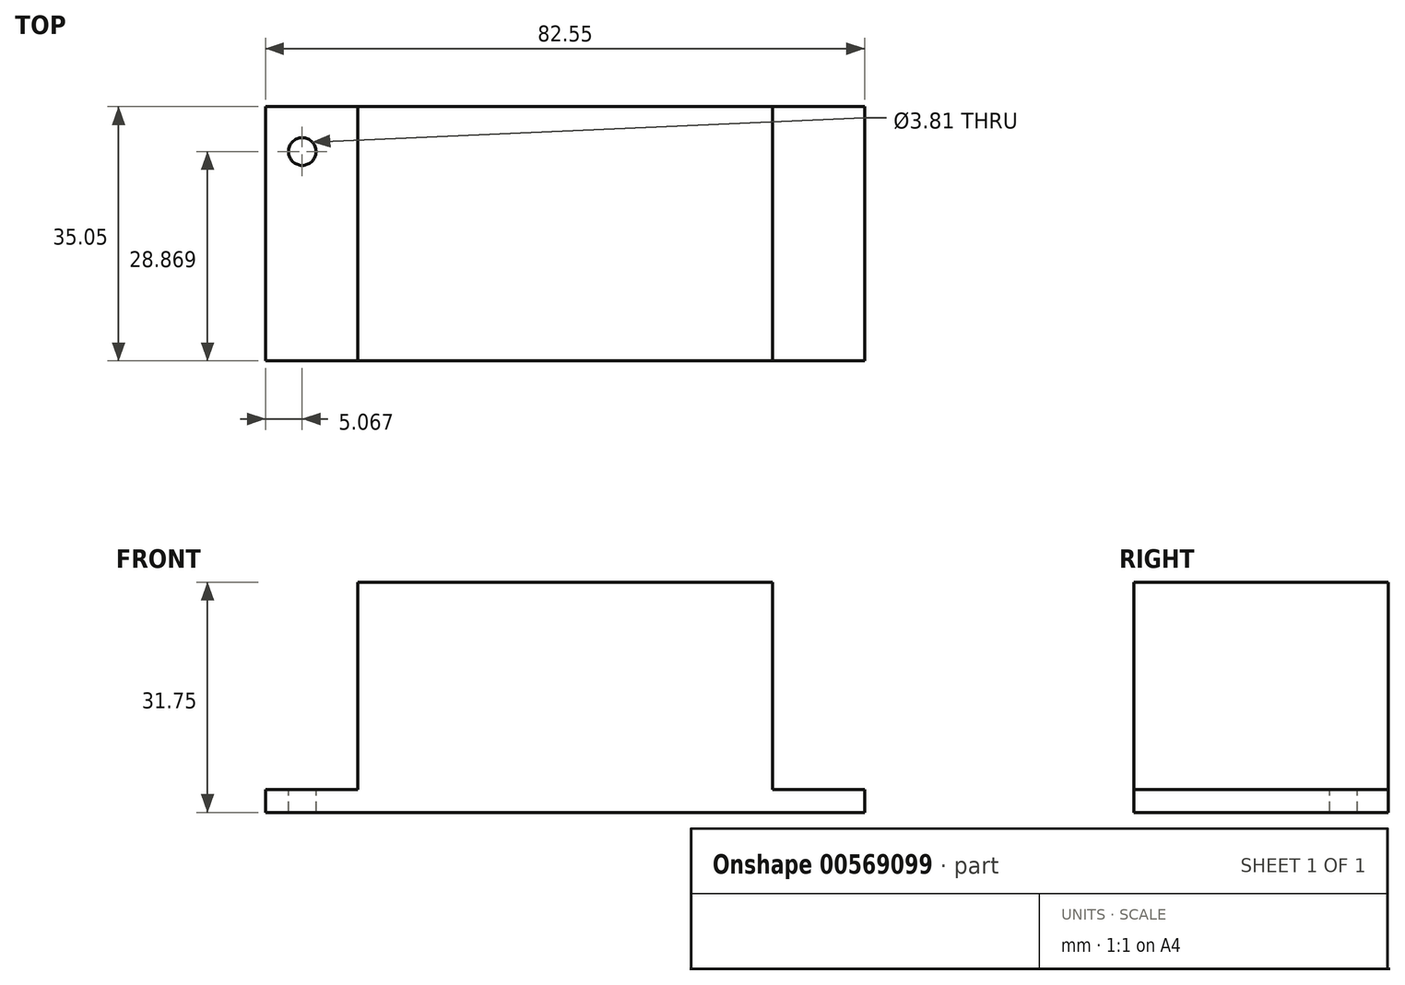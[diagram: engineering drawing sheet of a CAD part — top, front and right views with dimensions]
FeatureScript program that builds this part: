
annotation { "Feature Type Name" : "Feature", "Feature Type Description" : "" }
export const myFeature = defineFeature(function(context is Context, id is Id, definition is map)
    precondition{}
    {
        {
            var Q0;
            Q0=qCreatedBy(makeId("Top.planeOp"),FACE);
            var sketch = newSketch(context, id + "F0", { "sketchPlane" : qUnion([Q0])});
            skLineSegment(sketch, "E0.bottom", {"start": v(-39.5, -2.51) * mm, "end": v(43.04, -2.51) * mm});
            skLineSegment(sketch, "E0.top", {"start": v(-39.5, -37.56) * mm, "end": v(43.04, -37.56) * mm});
            skLineSegment(sketch, "E0.left", {"start": v(-39.5, -2.51) * mm, "end": v(-39.5, -37.56) * mm});
            skLineSegment(sketch, "E0.right", {"start": v(43.04, -2.51) * mm, "end": v(43.04, -37.56) * mm});
            skSolve(sketch);
        }
        {
            var Q0;
            Q0=makeQuery(id+"F0.imprint","IMPRINT",FACE,{"disambiguationData":[TD([[makeQuery(id+"F0.imprint","IMPRINT",EDGE,{"derivedFrom":sQuery(id+"F0.wireOp",EDGE,"E0.bottom")}),-1.0]])]});
            extrude(context, id + "F1", {"entities" : qUnion([Q0]), "depth" : 3.17 * mm, "offsetDistance" : 25.4 * mm});
        }
        {
            var Q0;
            Q0=makeQuery(id+"F1.opExtrude","CAP_FACE",FACE,{"disambiguationData":[OSD([sQuery(id+"F0.wireOp",EDGE,"E0.bottom"),sQuery(id+"F0.wireOp",EDGE,"E0.top"),sQuery(id+"F0.wireOp",EDGE,"E0.left"),sQuery(id+"F0.wireOp",EDGE,"E0.right")])],"isStart":false});
            var sketch = newSketch(context, id + "F2", { "sketchPlane" : qUnion([Q0])});
            skPoint(sketch, "E1", {"position": v(-34.44, -8.7) * mm});
            skSolve(sketch);
        }
        {
            var Q0;
            Q0=sQuery(id+"F2.wireOp",VERTEX,"E1");
            var Q1;
            Q1=makeQuery(id+"F1.opExtrude","SWEPT_BODY",BODY,{"disambiguationData":[OSD([sQuery(id+"F0.wireOp",EDGE,"E0.bottom"),sQuery(id+"F0.wireOp",EDGE,"E0.top"),sQuery(id+"F0.wireOp",EDGE,"E0.left"),sQuery(id+"F0.wireOp",EDGE,"E0.right")])]});
            hole(context, id + "F3", {"style" : HoleStyle.SIMPLE, "endStyle" : HoleEndStyle.THROUGH, "holeDiameter" : 3.8 * mm, "isTappedThrough" : true, "tappedDepth" : 12.7 * mm, "tapClearance" : 3, "locations" : qUnion([Q0]), "scope" : qUnion([Q1])});
        }
        {
            var Q0;
            Q0=qCreatedBy(makeId("Top.planeOp"),FACE);
            var sketch = newSketch(context, id + "F4", { "sketchPlane" : qUnion([Q0])});
            skLineSegment(sketch, "E2.bottom", {"start": v(-26.8, -2.51) * mm, "end": v(30.34, -2.51) * mm});
            skLineSegment(sketch, "E2.top", {"start": v(-26.8, -37.56) * mm, "end": v(30.34, -37.56) * mm});
            skLineSegment(sketch, "E2.left", {"start": v(-26.8, -2.51) * mm, "end": v(-26.8, -37.56) * mm});
            skLineSegment(sketch, "E2.right", {"start": v(30.34, -2.51) * mm, "end": v(30.34, -37.56) * mm});
            skSolve(sketch);
        }
        {
            var Q0;
            Q0 = qSketchRegion(id + "F4", true);
            extrude(context, id + "F5", {"entities" : qUnion([Q0]), "operationType" : NewBodyOperationType.ADD, "depth" : 31.75 * mm, "offsetDistance" : 25.4 * mm});
        }
    });
